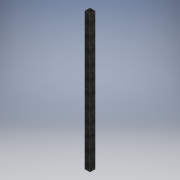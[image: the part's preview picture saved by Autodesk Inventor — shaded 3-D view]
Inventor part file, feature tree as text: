
AUTODESK INVENTOR PART (.ipt)
format: ipt  version: 2017 (Build 210142000, 142)  size: 104,960 bytes
history: native  units: mm
features: other x1, extrude x1, sketch x1
ambient origin geometry x8: Origin, YZ Plane, XZ Plane, XY Plane, X Axis, Y Axis, Z Axis, Center Point
bodies: Body1 (feature_tree)
feature tree (3):
  other  "Sólido1"
  extrude  "Extrusión1"  Depth=75.0mm
  sketch  "Boceto1"  dims[d0=75.0mm d1=75.0mm d2=3.0mm d3=37.5mm d4=37.5mm d5=1950.0mm d6=0.0mm]
